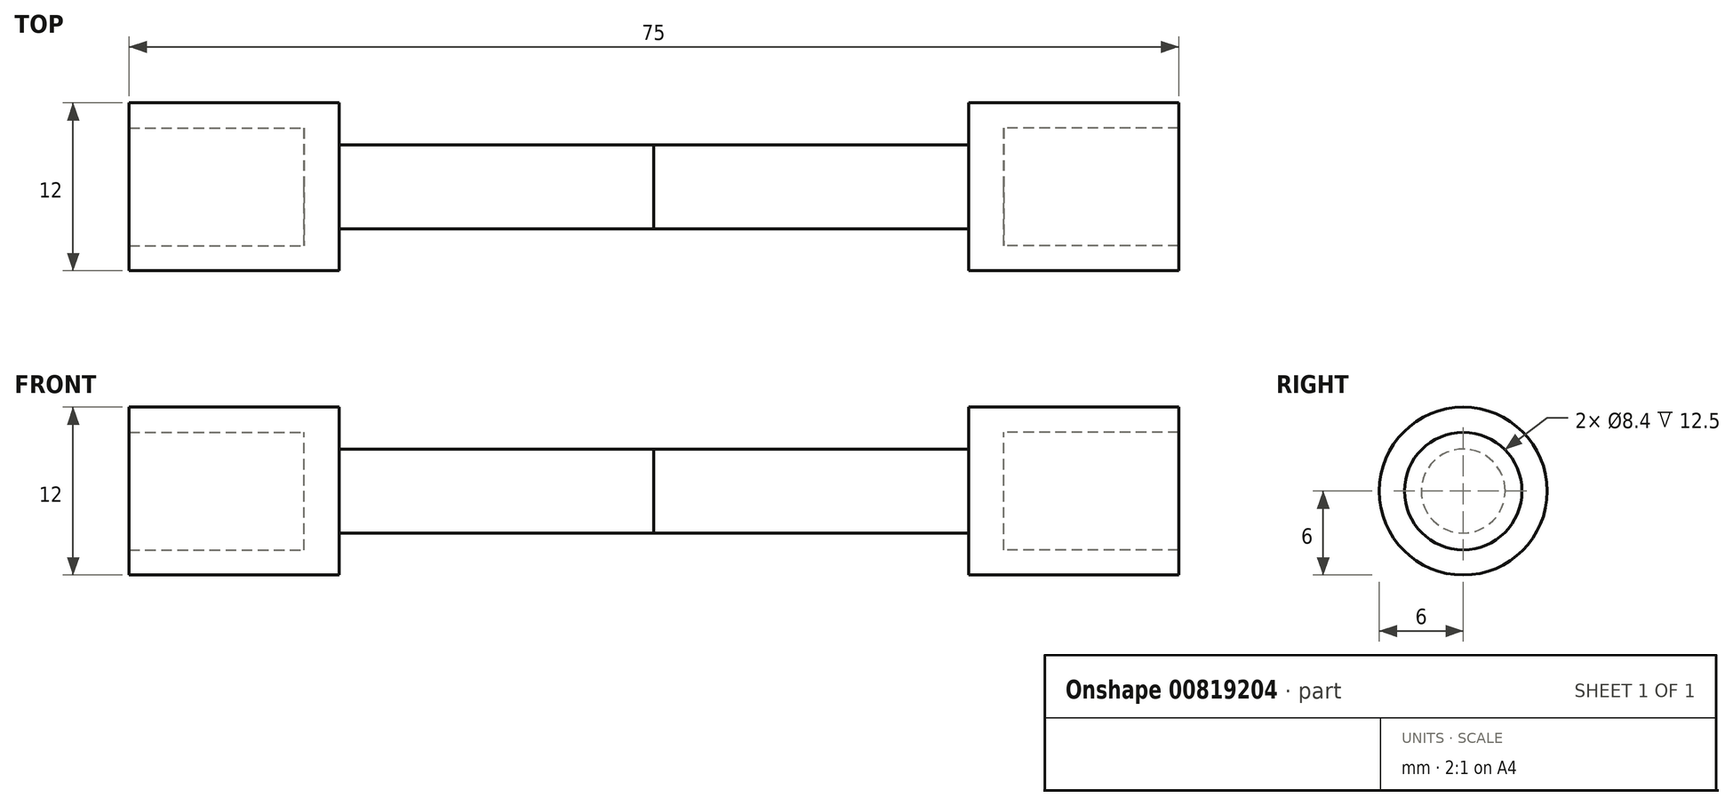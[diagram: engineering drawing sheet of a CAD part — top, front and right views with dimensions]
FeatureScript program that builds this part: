
annotation { "Feature Type Name" : "Feature", "Feature Type Description" : "" }
export const myFeature = defineFeature(function(context is Context, id is Id, definition is map)
    precondition{}
    {
        {
            var Q0;
            Q0=qCreatedBy(makeId("Right.planeOp"),FACE);
            var sketch = newSketch(context, id + "F0", { "sketchPlane" : qUnion([Q0])});
            skCircle(sketch, "E0", {"center": v(0, 0) * mm, "radius": 4.2 * mm});
            skCircle(sketch, "E1", {"center": v(0, 0) * mm, "radius": 6 * mm});
            skCircle(sketch, "E2", {"center": v(0, 0) * mm, "radius": 3 * mm});
            skSolve(sketch);
        }
        {
            var Q0;
            Q0=makeQuery(id+"F0.imprint","IMPRINT",FACE,{"disambiguationData":[TD([[makeQuery(id+"F0.imprint","IMPRINT",EDGE,{"derivedFrom":sQuery(id+"F0.wireOp",EDGE,"E0")}),-1.0]])]});
            extrude(context, id + "F1", {"entities" : qUnion([Q0]), "depth" : 12.5 * mm, "offsetDistance" : 25 * mm});
        }
        {
            var Q0;
            Q0=makeQuery(id+"F0.imprint","IMPRINT",FACE,{"disambiguationData":[TD([[makeQuery(id+"F0.imprint","IMPRINT",EDGE,{"derivedFrom":sQuery(id+"F0.wireOp",EDGE,"E0")}),1.0]])]});
            var Q1;
            Q1=makeQuery(id+"F0.imprint","IMPRINT",FACE,{"disambiguationData":[TD([[makeQuery(id+"F0.imprint","IMPRINT",EDGE,{"derivedFrom":sQuery(id+"F0.wireOp",EDGE,"E0")}),-1.0]])]});
            extrude(context, id + "F2", {"entities" : qUnion([Q0, Q1]), "operationType" : NewBodyOperationType.ADD, "oppositeDirection" : true, "depth" : 2.5 * mm, "offsetDistance" : 25 * mm});
        }
        {
            var Q0;
            Q0 = qSketchRegion(id + "F5", true);
            var Q1;
            Q1=makeQuery(id+"F0.imprint","IMPRINT",FACE,{"disambiguationData":[TD([[makeQuery(id+"F0.imprint","IMPRINT",EDGE,{"derivedFrom":sQuery(id+"F0.wireOp",EDGE,"E2")}),1.0]])]});
            extrude(context, id + "F3", {"entities" : qUnion([Q0, Q1]), "operationType" : NewBodyOperationType.ADD, "oppositeDirection" : true, "depth" : 25 * mm, "offsetDistance" : 25 * mm});
        }
        {
            var Q0;
            Q0=makeQuery(id+"F1.opExtrude","SWEPT_BODY",BODY,{"disambiguationData":[OSD([sQuery(id+"F0.wireOp",EDGE,"E0"),sQuery(id+"F0.wireOp",EDGE,"E1")])]});
            var Q1;
            Q1=makeQuery(id+"F3.opExtrude","CAP_FACE",FACE,{"disambiguationData":[OSD([sQuery(id+"F0.wireOp",EDGE,"E2")])],"isStart":false});
            mirror(context, id + "F4", {"entities" : qUnion([Q0]), "mirrorPlane" : qUnion([Q1])});
        }
    });
